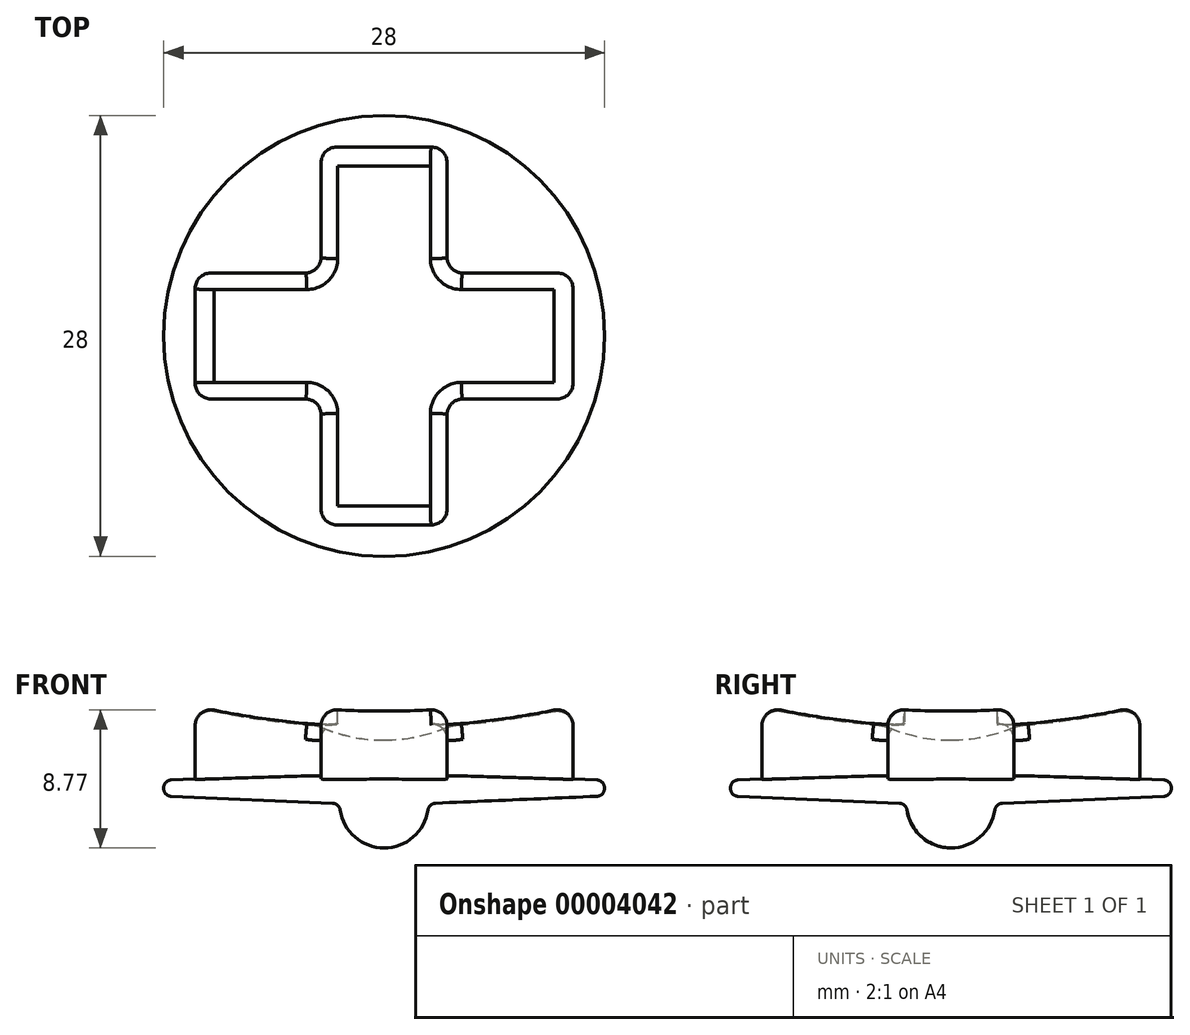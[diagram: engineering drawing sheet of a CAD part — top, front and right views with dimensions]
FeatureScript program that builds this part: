
annotation { "Feature Type Name" : "Feature", "Feature Type Description" : "" }
export const myFeature = defineFeature(function(context is Context, id is Id, definition is map)
    precondition{}
    {
        {
            var Q0;
            Q0=qCreatedBy(makeId("Top.planeOp"),FACE);
            var sketch = newSketch(context, id + "F0", { "sketchPlane" : qUnion([Q0])});
            skCircle(sketch, "E0", {"center": v(0, 0) * mm, "radius": 14 * mm});
            skSolve(sketch);
        }
        {
            var Q0;
            Q0=makeQuery(id+"F0.imprint","IMPRINT",FACE,{"disambiguationData":[TD([[makeQuery(id+"F0.imprint","IMPRINT",EDGE,{"derivedFrom":sQuery(id+"F0.wireOp",EDGE,"E0")}),1.0]])]});
            extrude(context, id + "F1", {"entities" : qUnion([Q0]), "depth" : 1 * mm});
        }
        {
            var Q0;
            Q0=makeQuery(id+"F1.opExtrude","CAP_FACE",FACE,{"disambiguationData":[OSD([sQuery(id+"F0.wireOp",EDGE,"E0")])],"isStart":false});
            var sketch = newSketch(context, id + "F2", { "sketchPlane" : qUnion([Q0])});
            skLineSegment(sketch, "E1", {"start": v(-4, 12) * mm, "end": v(0, 12) * mm});
            skLineSegment(sketch, "E2", {"start": v(0, 12) * mm, "end": v(4, 12) * mm});
            skLineSegment(sketch, "E3", {"start": v(4, 12) * mm, "end": v(4, 4) * mm});
            skLineSegment(sketch, "E4", {"start": v(4, 4) * mm, "end": v(12, 4) * mm});
            skLineSegment(sketch, "E5", {"start": v(12, 4) * mm, "end": v(12, 0) * mm});
            skLineSegment(sketch, "E6", {"start": v(12, 0) * mm, "end": v(12, -4) * mm});
            skLineSegment(sketch, "E7", {"start": v(12, -4) * mm, "end": v(4, -4) * mm});
            skLineSegment(sketch, "E8", {"start": v(4, -12) * mm, "end": v(0, -12) * mm});
            skLineSegment(sketch, "E9", {"start": v(0, -12) * mm, "end": v(-4, -12) * mm});
            skLineSegment(sketch, "E10", {"start": v(-4, -12) * mm, "end": v(-4, -4) * mm});
            skLineSegment(sketch, "E11", {"start": v(-4, -4) * mm, "end": v(-12, -4) * mm});
            skLineSegment(sketch, "E12", {"start": v(-12, -4) * mm, "end": v(-12, 0) * mm});
            skLineSegment(sketch, "E13", {"start": v(-12, 0) * mm, "end": v(-12, 4) * mm});
            skLineSegment(sketch, "E14", {"start": v(-12, 4) * mm, "end": v(-4, 4) * mm});
            skLineSegment(sketch, "E15", {"start": v(-4, 4) * mm, "end": v(-4, 12) * mm});
            skLineSegment(sketch, "E16", {"start": v(-4, 4) * mm, "end": v(0, 0) * mm, "construction": true});
            skLineSegment(sketch, "E17", {"start": v(0, 0) * mm, "end": v(4, 4) * mm, "construction": true});
            skLineSegment(sketch, "E18", {"start": v(0, 0) * mm, "end": v(4, -4) * mm, "construction": true});
            skLineSegment(sketch, "E19", {"start": v(0, 0) * mm, "end": v(-4, -4) * mm, "construction": true});
            skLineSegment(sketch, "E20", {"start": v(4, -4) * mm, "end": v(4, -12) * mm});
            skSolve(sketch);
        }
        {
            var Q0;
            Q0=makeQuery(id+"F2.imprint","IMPRINT",FACE,{"disambiguationData":[TD([[makeQuery(id+"F2.imprint","IMPRINT",EDGE,{"derivedFrom":sQuery(id+"F2.wireOp",EDGE,"E1")}),-1.0]])]});
            extrude(context, id + "F3", {"entities" : qUnion([Q0]), "operationType" : NewBodyOperationType.ADD, "depth" : 4.8 * mm});
        }
        {
            var Q0;
            Q0=qCreatedBy(makeId("Front.planeOp"),FACE);
            var sketch = newSketch(context, id + "F4", { "sketchPlane" : qUnion([Q0])});
            skLineSegment(sketch, "E21", {"start": v(0, 4.3) * mm, "end": v(0, 5.8) * mm});
            skLineSegment(sketch, "E22", {"start": v(0, 5.8) * mm, "end": v(-12.75, 5.8) * mm});
            skArc(sketch, "E23", {"start": v(-12.75, 5.8) * mm, "mid": v(-6.42, 4.68) * mm, "end": v(0, 4.3) * mm});
            skLineSegment(sketch, "E24", {"start": v(0, 4.3) * mm, "end": v(0, 3.55) * mm});
            skLineSegment(sketch, "E25", {"start": v(0, 3.55) * mm, "end": v(0, 0) * mm, "construction": true});
            skArc(sketch, "E26", {"start": v(-4.25, 4.46) * mm, "mid": v(-2.17, 3.78) * mm, "end": v(0, 3.55) * mm});
            skSolve(sketch);
        }
        {
            var Q0;
            {var subQ2=sQuery(id+"F4.wireOp",EDGE,"E21");Q0=makeQuery(id+"F4.imprint","IMPRINT",FACE,{"disambiguationData":[TD([[makeQuery(id+"F4.imprint","IMPRINT",EDGE,{"derivedFrom":subQ2}),1.0]])]});}
            var Q1;
            {var subQ1=sQuery(id+"F4.wireOp",EDGE,"E24");Q1=makeQuery(id+"F4.imprint","IMPRINT",FACE,{"disambiguationData":[TD([[makeQuery(id+"F4.imprint","IMPRINT",EDGE,{"derivedFrom":subQ1}),-1.0]])]});}
            var Q2;
            Q2=sQuery(id+"F4.wireOp",EDGE,"E24");
            revolve(context, id + "F5", {"operationType" : NewBodyOperationType.REMOVE, "entities" : qUnion([Q0, Q1]), "axis" : qUnion([Q2]), "revolveType" : RevolveType.FULL, "oppositeDirection" : true});
        }
        {
            var Q0;
            Q0=qCreatedBy(makeId("Front.planeOp"),FACE);
            var sketch = newSketch(context, id + "F6", { "sketchPlane" : qUnion([Q0])});
            skLineSegment(sketch, "E27.0", {"start": v(-14, 1) * mm, "end": v(14, 1) * mm});
            skLineSegment(sketch, "E28", {"start": v(0, 0) * mm, "end": v(0, 1) * mm, "construction": true});
            skLineSegment(sketch, "E29", {"start": v(0, 1) * mm, "end": v(0, 1.5) * mm});
            skLineSegment(sketch, "E30", {"start": v(0, 1.5) * mm, "end": v(-14, 1) * mm});
            skSolve(sketch);
        }
        {
            var Q0;
            {var subQ1=sQuery(id+"F6.wireOp",EDGE,"E29");Q0=makeQuery(id+"F6.imprint","IMPRINT",FACE,{"disambiguationData":[TD([[makeQuery(id+"F6.imprint","IMPRINT",EDGE,{"derivedFrom":subQ1}),1.0]])]});}
            var Q1;
            Q1=sQuery(id+"F6.wireOp",EDGE,"E29");
            revolve(context, id + "F7", {"operationType" : NewBodyOperationType.ADD, "entities" : qUnion([Q0]), "axis" : qUnion([Q1]), "revolveType" : RevolveType.FULL});
        }
        {
            var Q0;
            Q0=makeQuery(id+"F3.opExtrude","SWEPT_EDGE",EDGE,{"disambiguationData":[OSD([sQuery(id+"F2.wireOp",EDGE,"E3"),sQuery(id+"F2.wireOp",EDGE,"E4")])]});
            var Q1;
            Q1=makeQuery(id+"F3.opExtrude","SWEPT_EDGE",EDGE,{"disambiguationData":[OSD([sQuery(id+"F2.wireOp",EDGE,"E4"),sQuery(id+"F2.wireOp",EDGE,"E5")])]});
            var Q2;
            Q2=makeQuery(id+"F3.opExtrude","SWEPT_EDGE",EDGE,{"disambiguationData":[OSD([sQuery(id+"F2.wireOp",EDGE,"E2"),sQuery(id+"F2.wireOp",EDGE,"E3")])]});
            var Q3;
            Q3=makeQuery(id+"F3.opExtrude","SWEPT_EDGE",EDGE,{"disambiguationData":[OSD([sQuery(id+"F2.wireOp",EDGE,"E1"),sQuery(id+"F2.wireOp",EDGE,"E15")])]});
            var Q4;
            Q4=makeQuery(id+"F3.opExtrude","SWEPT_EDGE",EDGE,{"disambiguationData":[OSD([sQuery(id+"F2.wireOp",EDGE,"E14"),sQuery(id+"F2.wireOp",EDGE,"E15")])]});
            var Q5;
            Q5=makeQuery(id+"F3.opExtrude","SWEPT_EDGE",EDGE,{"disambiguationData":[OSD([sQuery(id+"F2.wireOp",EDGE,"E13"),sQuery(id+"F2.wireOp",EDGE,"E14")])]});
            var Q6;
            Q6=makeQuery(id+"F3.opExtrude","SWEPT_EDGE",EDGE,{"disambiguationData":[OSD([sQuery(id+"F2.wireOp",EDGE,"E11"),sQuery(id+"F2.wireOp",EDGE,"E12")])]});
            var Q7;
            Q7=makeQuery(id+"F3.opExtrude","SWEPT_EDGE",EDGE,{"disambiguationData":[OSD([sQuery(id+"F2.wireOp",EDGE,"E10"),sQuery(id+"F2.wireOp",EDGE,"E11")])]});
            var Q8;
            Q8=makeQuery(id+"F3.opExtrude","SWEPT_EDGE",EDGE,{"disambiguationData":[OSD([sQuery(id+"F2.wireOp",EDGE,"E9"),sQuery(id+"F2.wireOp",EDGE,"E10")])]});
            var Q9;
            Q9=makeQuery(id+"F3.opExtrude","SWEPT_EDGE",EDGE,{"disambiguationData":[OSD([sQuery(id+"F2.wireOp",EDGE,"E8"),sQuery(id+"F2.wireOp",EDGE,"E20")])]});
            var Q10;
            Q10=makeQuery(id+"F3.opExtrude","SWEPT_EDGE",EDGE,{"disambiguationData":[OSD([sQuery(id+"F2.wireOp",EDGE,"E7"),sQuery(id+"F2.wireOp",EDGE,"E20")])]});
            var Q11;
            Q11=makeQuery(id+"F3.opExtrude","SWEPT_EDGE",EDGE,{"disambiguationData":[OSD([sQuery(id+"F2.wireOp",EDGE,"E6"),sQuery(id+"F2.wireOp",EDGE,"E7")])]});
            fillet(context, id + "F8", {"entities" : qUnion([Q0, Q1, Q2, Q3, Q4, Q5, Q6, Q7, Q8, Q9, Q10, Q11]), "radius" : 1 * mm, "allowEdgeOverflow" : false});
        }
        {
            var Q0;
            Q0=makeQuery(id+"F5.boolean.opBoolean","COPY",EDGE,{"derivedFrom":makeQuery(id+"F5.opRevolve","SWEPT_EDGE",EDGE,{"disambiguationData":[OSD([sQuery(id+"F4.wireOp",EDGE,"E23"),sQuery(id+"F4.wireOp",EDGE,"E26")])]})});
            fillet(context, id + "F9", {"entities" : qUnion([Q0]), "radius" : 2 * mm, "tangentPropagation" : true, "allowEdgeOverflow" : false});
        }
        {
            var Q0;
            Q0=qCreatedBy(makeId("Right.planeOp"),FACE);
            var sketch = newSketch(context, id + "F10", { "sketchPlane" : qUnion([Q0])});
            skLineSegment(sketch, "E31.0", {"start": v(-14, 0) * mm, "end": v(14, 0) * mm, "construction": true});
            skLineSegment(sketch, "E32", {"start": v(-14, 0) * mm, "end": v(0, 0) * mm});
            skLineSegment(sketch, "E33", {"start": v(0, 0) * mm, "end": v(0, -0.6) * mm});
            skLineSegment(sketch, "E34", {"start": v(-14, 0) * mm, "end": v(0, -0.6) * mm});
            skLineSegment(sketch, "E35", {"start": v(0, -0.6) * mm, "end": v(0, -3.3) * mm});
            skArc(sketch, "E36", {"start": v(-2.82, -0.48) * mm, "mid": v(-2, -2.47) * mm, "end": v(0, -3.3) * mm});
            skSolve(sketch);
        }
        {
            var Q0;
            Q0=qSketchRegion(id+"F10",true);
            var Q1;
            Q1=sQuery(id+"F10.wireOp",EDGE,"E33");
            revolve(context, id + "F11", {"operationType" : NewBodyOperationType.ADD, "entities" : qUnion([Q0]), "axis" : qUnion([Q1]), "revolveType" : RevolveType.FULL});
        }
        {
            var Q0;
            Q0=makeQuery(id+"F11.boolean.opBoolean","MERGE",EDGE,{"derivedFrom":[makeQuery(id+"F1.opExtrude","CAP_EDGE",EDGE,{"disambiguationData":[OSD([sQuery(id+"F0.wireOp",EDGE,"E0")])],"isStart":true}),makeQuery(id+"F11.opRevolve","SWEPT_EDGE",EDGE,{"disambiguationData":[OSD([sQuery(id+"F10.wireOp",EDGE,"E32"),sQuery(id+"F10.wireOp",EDGE,"E34")])]})]});
            var Q1;
            Q1=makeQuery(id+"F11.opRevolve","SWEPT_EDGE",EDGE,{"disambiguationData":[OSD([sQuery(id+"F10.wireOp",EDGE,"E34"),sQuery(id+"F10.wireOp",EDGE,"E36")])]});
            var Q2;
            Q2=makeQuery(id+"F7.boolean.opBoolean","MERGE",EDGE,{"derivedFrom":[makeQuery(id+"F1.opExtrude","CAP_EDGE",EDGE,{"disambiguationData":[OSD([sQuery(id+"F0.wireOp",EDGE,"E0")])],"isStart":false}),makeQuery(id+"F7.opRevolve","SWEPT_EDGE",EDGE,{"disambiguationData":[OSD([sQuery(id+"F6.wireOp",EDGE,"E27.0"),sQuery(id+"F6.wireOp",EDGE,"E30")])]})]});
            fillet(context, id + "F12", {"entities" : qUnion([Q0, Q1, Q2]), "radius" : .50 * mm, "tangentPropagation" : true, "allowEdgeOverflow" : false});
        }
        {
            var Q0;
            Q0=makeQuery(id+"F5.boolean.opBoolean","INTERSECT",EDGE,{"derivedFrom":[makeQuery(id+"F3.opExtrude","SWEPT_FACE",FACE,{"disambiguationData":[OSD([sQuery(id+"F2.wireOp",EDGE,"E14")])]}),makeQuery(id+"F5.opRevolve","SWEPT_FACE",FACE,{"disambiguationData":[OSD([sQuery(id+"F4.wireOp",EDGE,"E23")])]})]});
            var Q1;
            Q1=makeQuery(id+"F5.boolean.opBoolean","INTERSECT",EDGE,{"derivedFrom":[makeQuery(id+"F3.opExtrude","SWEPT_FACE",FACE,{"disambiguationData":[OSD([sQuery(id+"F2.wireOp",EDGE,"E11")])]}),makeQuery(id+"F5.opRevolve","SWEPT_FACE",FACE,{"disambiguationData":[OSD([sQuery(id+"F4.wireOp",EDGE,"E23")])]})]});
            var Q2;
            Q2=makeQuery(id+"F5.boolean.opBoolean","INTERSECT",EDGE,{"derivedFrom":[makeQuery(id+"F3.opExtrude","SWEPT_FACE",FACE,{"disambiguationData":[OSD([sQuery(id+"F2.wireOp",EDGE,"E10")])]}),makeQuery(id+"F5.opRevolve","SWEPT_FACE",FACE,{"disambiguationData":[OSD([sQuery(id+"F4.wireOp",EDGE,"E23")])]})]});
            var Q3;
            Q3=makeQuery(id+"F5.boolean.opBoolean","INTERSECT",EDGE,{"derivedFrom":[makeQuery(id+"F3.opExtrude","SWEPT_FACE",FACE,{"disambiguationData":[OSD([sQuery(id+"F2.wireOp",EDGE,"E20")])]}),makeQuery(id+"F5.opRevolve","SWEPT_FACE",FACE,{"disambiguationData":[OSD([sQuery(id+"F4.wireOp",EDGE,"E23")])]})]});
            var Q4;
            Q4=makeQuery(id+"F5.boolean.opBoolean","INTERSECT",EDGE,{"derivedFrom":[makeQuery(id+"F3.opExtrude","SWEPT_FACE",FACE,{"disambiguationData":[OSD([sQuery(id+"F2.wireOp",EDGE,"E7")])]}),makeQuery(id+"F5.opRevolve","SWEPT_FACE",FACE,{"disambiguationData":[OSD([sQuery(id+"F4.wireOp",EDGE,"E23")])]})]});
            var Q5;
            Q5=makeQuery(id+"F5.boolean.opBoolean","INTERSECT",EDGE,{"derivedFrom":[makeQuery(id+"F3.opExtrude","SWEPT_FACE",FACE,{"disambiguationData":[OSD([sQuery(id+"F2.wireOp",EDGE,"E3")])]}),makeQuery(id+"F5.opRevolve","SWEPT_FACE",FACE,{"disambiguationData":[OSD([sQuery(id+"F4.wireOp",EDGE,"E23")])]})]});
            var Q6;
            Q6=makeQuery(id+"F5.boolean.opBoolean","INTERSECT",EDGE,{"derivedFrom":[makeQuery(id+"F3.opExtrude","SWEPT_FACE",FACE,{"disambiguationData":[OSD([sQuery(id+"F2.wireOp",EDGE,"E15")])]}),makeQuery(id+"F5.opRevolve","SWEPT_FACE",FACE,{"disambiguationData":[OSD([sQuery(id+"F4.wireOp",EDGE,"E23")])]})]});
            var Q7;
            Q7=makeQuery(id+"F5.boolean.opBoolean","INTERSECT",EDGE,{"derivedFrom":[makeQuery(id+"F3.opExtrude","SWEPT_FACE",FACE,{"disambiguationData":[OSD([sQuery(id+"F2.wireOp",EDGE,"E4")])]}),makeQuery(id+"F5.opRevolve","SWEPT_FACE",FACE,{"disambiguationData":[OSD([sQuery(id+"F4.wireOp",EDGE,"E23")])]})]});
            fillet(context, id + "F13", {"entities" : qUnion([Q0, Q1, Q2, Q3, Q4, Q5, Q6, Q7]), "radius" : 1 * mm, "tangentPropagation" : true, "allowEdgeOverflow" : false});
        }
    });
